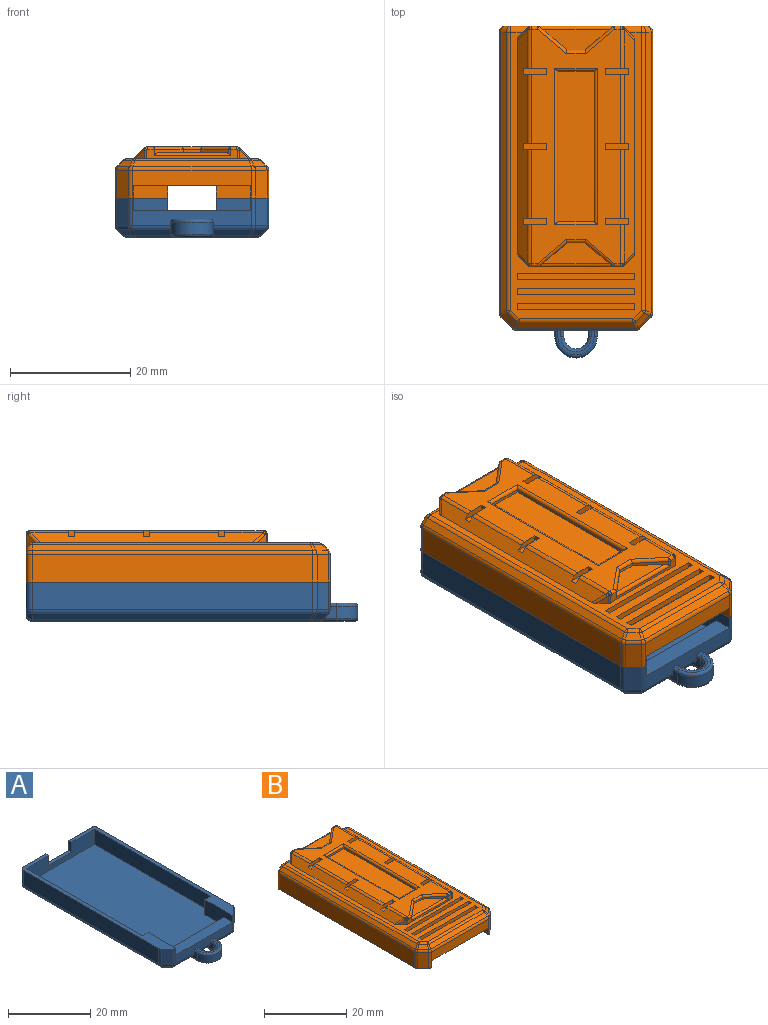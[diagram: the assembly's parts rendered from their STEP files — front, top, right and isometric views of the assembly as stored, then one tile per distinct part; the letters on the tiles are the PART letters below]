
ASSEMBLY  parts=2 mates=1
PART A: 149 faces, bbox 25.5x55.4x6.5 mm
  f0: plane 19.67x4.59mm, normal (0,-1,0), area 48.2mm2, adj f3,f4,f12,f14,f21,f22,f23,f35
  f1: plane 6.39x0.92mm, normal (0,-0.71,-0.71), area 8mm2, adj f3,f5,f62,f131,f137
  f2: plane 4.09x0.92mm, normal (0,-0.71,-0.71), area 5.2mm2, adj f4,f6,f132,f134,f140,f142
  f3: cylinder r=1mm len=6.34mm, axis (1,0,0), area 5mm2, adj f0,f1,f61,f131
  f4: cylinder r=1mm len=4mm, axis (1,0,0), area 3.1mm2, adj f0,f2,f132,f134
  f5: cylinder r=1mm len=6.46mm, axis (1,0,0), area 4.9mm2, adj f1,f7,f63,f137
  f6: cylinder r=1mm len=5mm, axis (1,0,0), area 3.5mm2, adj f2,f7,f140,f142
  f7: plane 53.59x21.67mm, normal (0,0,-1), area 887.7mm2, adj f5,f6,f38,f39,f40,f41,f42,f47
  f8: plane 40x4.5mm, normal (1,0,0), area 180mm2, adj f9,f14,f17,f25
  f9: plane 46.5x23.5mm, normal (0,0,1), area 1066.8mm2, adj f8,f10,f11,f17,f22,f23,f24,f25
  f10: plane 19.5x2.5mm, normal (0,1,0), area 48.7mm2, adj f9,f21,f22,f23
  f11: plane 40x4.5mm, normal (-1,0,0), area 180mm2, adj f9,f12,f17,f24
  f12: plane 50.5x8.75mm, normal (0,0,1), area 73.9mm2, adj f0,f11,f13,f15,f17,f20,f22,f24
  f13: plane 23.5x5.5mm, normal (0,1,0), area 104.4mm2, adj f12,f14,f18,f19,f20,f43,f45,f47
  f14: plane 50.5x8.75mm, normal (0,0,1), area 73.9mm2, adj f0,f8,f13,f16,f17,f19,f23,f25
  f15: plane 46.59x4.59mm, normal (1,0,0), area 213.6mm2, adj f12,f33,f51,f64
  f16: plane 46.59x4.59mm, normal (-1,0,0), area 213.6mm2, adj f14,f37,f43,f56
  f17: plane 23.5x4.5mm, normal (0,-1,0), area 81.7mm2, adj f8,f9,f11,f12,f14,f18,f19,f20
  f18: plane 8x1mm, normal (0,0,1), area 8mm2, adj f13,f17,f19,f20
  f19: plane 3x1mm, normal (1,0,0), area 3mm2, adj f13,f14,f17,f18
  f20: plane 3x1mm, normal (-1,0,0), area 3mm2, adj f12,f13,f17,f18
  f21: plane 19.5x3mm, normal (0,0,1), area 58.5mm2, adj f0,f10,f22,f23
  f22: plane 9.5x4.5mm, normal (-1,0,0), area 35.2mm2, adj f0,f9,f10,f12,f21,f24
  f23: plane 9.5x4.5mm, normal (1,0,0), area 35.2mm2, adj f0,f9,f10,f14,f21,f25
  f24: plane 4.5x2mm, normal (0,1,0), area 9mm2, adj f9,f11,f12,f22
  f25: plane 4.5x2mm, normal (0,1,0), area 9mm2, adj f8,f9,f14,f23
  f26: plane 4.59x1.91mm, normal (0.71,-0.71,0), area 12.4mm2, adj f12,f34,f52,f64
  f27: plane 4.59x1.91mm, normal (-0.71,-0.71,0), area 12.4mm2, adj f14,f36,f56,f60
  f28: plane 46.59x0.91mm, normal (0.71,0,-0.71), area 60mm2, adj f33,f42,f49,f66
  f29: plane 2.29x2.29mm, normal (0.5,-0.5,-0.71), area 3mm2, adj f34,f41,f54,f66
  f30: plane 6.39x0.92mm, normal (0,-0.71,-0.71), area 8mm2, adj f35,f40,f54,f135,f139
  f31: plane 46.59x0.91mm, normal (-0.71,0,-0.71), area 60mm2, adj f37,f38,f45,f58
  f32: plane 2.29x2.29mm, normal (-0.5,-0.5,-0.71), area 3mm2, adj f36,f39,f58,f62
  f33: cylinder r=1mm len=46.59mm, axis (0,1,0), area 36.6mm2, adj f15,f28,f50,f65
  f34: cylinder r=1mm len=2.12mm, axis (0.71,0.71,0), area 2.1mm2, adj f26,f29,f53,f65
  f35: cylinder r=1mm len=6.34mm, axis (1,0,0), area 5mm2, adj f0,f30,f53,f135
  f36: cylinder r=1mm len=2.12mm, axis (0.71,-0.71,0), area 2.1mm2, adj f27,f32,f57,f61
  f37: cylinder r=1mm len=46.59mm, axis (0,-1,0), area 36.6mm2, adj f16,f31,f44,f57
  f38: cylinder r=1mm len=46.21mm, axis (0,-1,0), area 36.3mm2, adj f7,f31,f46,f59
  f39: cylinder r=1mm len=1.88mm, axis (-0.71,0.71,0), area 1.5mm2, adj f7,f32,f59,f63
  f40: cylinder r=1mm len=6.46mm, axis (1,0,0), area 4.9mm2, adj f7,f30,f55,f139
  f41: cylinder r=1mm len=1.88mm, axis (0.71,0.71,0), area 1.5mm2, adj f7,f29,f55,f67
  f42: cylinder r=1mm len=46.21mm, axis (0,-1,0), area 36.3mm2, adj f7,f28,f48,f67
  f43: cylinder r=1mm len=4.59mm, axis (0,0,1), area 7.2mm2, adj f13,f14,f16,f44
  f44: sphere r=1mm, area 0.8mm2, adj f37,f43,f45
  f45: cylinder r=1mm len=1.62mm, axis (0.71,0,-0.71), area 2mm2, adj f13,f31,f44,f46
  f46: sphere r=1mm, area 0.8mm2, adj f38,f45,f47
  f47: cylinder r=1mm len=21.67mm, axis (-1,0,0), area 34mm2, adj f7,f13,f46,f48
  f48: sphere r=1mm, area 0.8mm2, adj f42,f47,f49
  f49: cylinder r=1mm len=1.62mm, axis (-0.71,0,-0.71), area 2mm2, adj f13,f28,f48,f50
  f50: sphere r=1mm, area 0.8mm2, adj f33,f49,f51
  f51: cylinder r=1mm len=4.59mm, axis (0,0,-1), area 7.2mm2, adj f12,f13,f15,f50
  f52: cylinder r=1mm len=4.59mm, axis (0,0,1), area 3.6mm2, adj f0,f12,f26,f53
  f53: sphere r=1mm, area 0.6mm2, adj f34,f35,f52,f54
  f54: cylinder r=1mm len=1.12mm, axis (0.28,-0.68,0.68), area 0.7mm2, adj f29,f30,f53,f55
  f55: sphere r=1mm, area 0.2mm2, adj f40,f41,f54
  f56: cylinder r=1mm len=4.59mm, axis (0,0,-1), area 3.6mm2, adj f14,f16,f27,f57
  f57: sphere r=1mm, area 0.6mm2, adj f36,f37,f56,f58
  f58: cylinder r=1mm len=1.12mm, axis (-0.68,-0.28,0.68), area 0.7mm2, adj f31,f32,f57,f59
  f59: sphere r=1mm, area 0.2mm2, adj f38,f39,f58
  f60: cylinder r=1mm len=4.59mm, axis (0,0,1), area 3.6mm2, adj f0,f14,f27,f61
  f61: sphere r=1mm, area 0.6mm2, adj f3,f36,f60,f62
  f62: cylinder r=1mm len=1.12mm, axis (0.28,0.68,-0.68), area 0.7mm2, adj f1,f32,f61,f63
  f63: sphere r=1mm, area 0.2mm2, adj f5,f39,f62
  f64: cylinder r=1mm len=4.59mm, axis (0,0,1), area 3.6mm2, adj f12,f15,f26,f65
  f65: sphere r=1mm, area 0.6mm2, adj f33,f34,f64,f66
  f66: cylinder r=1mm len=1.12mm, axis (-0.68,0.28,-0.68), area 0.7mm2, adj f28,f29,f65,f67
  f67: sphere r=1mm, area 0.2mm2, adj f41,f42,f66
  f68: plane 1.19x0.5mm, normal (1,0,0), area 0.6mm2, adj f7,f69,f79,f80
  f69: plane 4.93x3.64mm, normal (-0.59,-0.8,0), area 3.1mm2, adj f7,f68,f70,f80
  f70: plane 3.79x3.51mm, normal (0.68,-0.73,0), area 2.6mm2, adj f7,f69,f71,f80
  f71: plane 1.2x0.5mm, normal (-1,0,0), area 0.6mm2, adj f7,f70,f72,f80
  f72: plane 4.32x3.95mm, normal (-0.67,0.74,0), area 2.9mm2, adj f7,f71,f73,f80
  f73: plane 4.32x0.5mm, normal (0,-1,0), area 2.2mm2, adj f7,f72,f74,f80
  f74: plane 1.01x0.5mm, normal (-1,0,0), area 0.5mm2, adj f7,f73,f75,f80
  f75: plane 8.72x0.5mm, normal (0,1,0), area 4.4mm2, adj f7,f74,f76,f80
  f76: plane 1.01x0.5mm, normal (1,0,0), area 0.5mm2, adj f7,f75,f77,f80
  f77: plane 3.42x0.5mm, normal (0,-1,0), area 1.7mm2, adj f7,f76,f78,f80
  f78: plane 0.91x0.81mm, normal (0.75,-0.66,0), area 0.6mm2, adj f7,f77,f79,f80
  f79: plane 4.23x3.18mm, normal (0.6,0.8,0), area 2.6mm2, adj f7,f68,f78,f80
  f80: plane 8.72x6.3mm, normal (0,0,-1), area 20mm2, adj f68,f69,f70,f71,f72,f73,f74,f75
  f81: plane 2.5x0.5mm, normal (1,0,0), area 1.3mm2, adj f7,f82,f89,f126
  f82: plane 2.5x0.5mm, normal (0,1,0), area 1.3mm2, adj f7,f81,f89,f129
  f83: plane 5x0.5mm, normal (1,0,0), area 2.5mm2, adj f7,f89,f128,f129
  f84: plane 5x0.5mm, normal (0,-1,0), area 2.5mm2, adj f7,f89,f127,f128
  f85: plane 2.5x0.5mm, normal (-1,0,0), area 1.3mm2, adj f7,f86,f89,f127
  f86: plane 2.5x0.5mm, normal (0,-1,0), area 1.3mm2, adj f7,f85,f89,f125
  f87: plane 5x0.5mm, normal (-1,0,0), area 2.5mm2, adj f7,f89,f124,f125
  f88: plane 5x0.5mm, normal (0,1,0), area 2.5mm2, adj f7,f89,f124,f126
  f89: plane 10.5x10.5mm, normal (0,0,-1), area 84.5mm2, adj f81,f82,f83,f84,f85,f86,f87,f88
  f90: plane 8.72x0.5mm, normal (0,1,0), area 4.4mm2, adj f7,f91,f93,f94
  f91: plane 1.01x0.5mm, normal (1,0,0), area 0.5mm2, adj f7,f90,f92,f94
  f92: plane 8.72x0.5mm, normal (0,-1,0), area 4.4mm2, adj f7,f91,f93,f94
  f93: plane 1.01x0.5mm, normal (-1,0,0), area 0.5mm2, adj f7,f90,f92,f94
  f94: plane 8.72x1.01mm, normal (0,0,-1), area 8.8mm2, adj f90,f91,f92,f93
  f95: plane 4.86x0.5mm, normal (1,0,0), area 2.4mm2, adj f7,f96,f106,f107
  f96: plane 0.91x0.5mm, normal (0,-1,0), area 0.5mm2, adj f7,f95,f97,f107
  f97: plane 3.85x0.5mm, normal (-1,0,0), area 1.9mm2, adj f7,f96,f98,f107
  f98: plane 3.21x0.5mm, normal (0,-1,0), area 1.6mm2, adj f7,f97,f99,f107
  f99: plane 3.61x0.5mm, normal (1,0,0), area 1.8mm2, adj f7,f98,f100,f107
  f100: plane 0.9x0.5mm, normal (0,-1,0), area 0.4mm2, adj f7,f99,f101,f107
  f101: plane 3.61x0.5mm, normal (-1,0,0), area 1.8mm2, adj f7,f100,f102,f107
  f102: plane 2.81x0.5mm, normal (0,-1,0), area 1.4mm2, adj f7,f101,f103,f107
  f103: plane 3.85x0.5mm, normal (1,0,0), area 1.9mm2, adj f7,f102,f104,f107
  f104: plane 0.9x0.5mm, normal (0,-1,0), area 0.5mm2, adj f7,f103,f105,f107
  f105: plane 4.86x0.5mm, normal (-1,0,0), area 2.4mm2, adj f7,f104,f106,f107
  f106: plane 8.72x0.5mm, normal (0,1,0), area 4.4mm2, adj f7,f95,f105,f107
  f107: plane 8.72x4.86mm, normal (0,0,-1), area 19mm2, adj f95,f96,f97,f98,f99,f100,f101,f102
  f108: extruded ~2.27x0.96mm, area 1.3mm2, adj f7,f109,f122,f123
  f109: extruded ~1.98x0.5mm, area 1mm2, adj f7,f108,f110,f123
  f110: plane 0.87x0.5mm, normal (0.44,-0.9,0), area 0.5mm2, adj f7,f109,f111,f123
  f111: extruded ~2.4x0.5mm, area 1.2mm2, adj f7,f110,f112,f123
  f112: extruded ~2.24x0.55mm, area 1.2mm2, adj f7,f111,f113,f123
  f113: extruded ~1.56x1.46mm, area 1.1mm2, adj f7,f112,f114,f123
  f114: extruded ~2.36x0.5mm, area 1.2mm2, adj f7,f113,f115,f123
  f115: extruded ~3.32x1.05mm, area 1.8mm2, adj f7,f114,f116,f123
  f116: extruded ~2.97x1.17mm, area 1.6mm2, adj f7,f115,f117,f123
  f117: extruded ~2.24x0.5mm, area 1.1mm2, adj f7,f116,f118,f123
  f118: plane 0.89x0.5mm, normal (0,-1,0), area 0.4mm2, adj f7,f117,f119,f123
  f119: extruded ~2.08x0.5mm, area 1.1mm2, adj f7,f118,f120,f123
  f120: extruded ~2.29x0.93mm, area 1.3mm2, adj f7,f119,f121,f123
  f121: extruded ~2.64x0.8mm, area 1.4mm2, adj f7,f120,f122,f123
  f122: extruded ~2.62x0.83mm, area 1.4mm2, adj f7,f108,f121,f123
  f123: plane 8.96x6.6mm, normal (0,0,-1), area 16.6mm2, adj f108,f109,f110,f111,f112,f113,f114,f115
  f124: cylinder r=1mm len=1mm, axis (0,0,-1), area 0.8mm2, adj f7,f87,f88,f89
  f125: cylinder r=1mm len=1mm, axis (0,0,1), area 0.8mm2, adj f7,f86,f87,f89
  f126: cylinder r=1mm len=1mm, axis (0,0,1), area 0.8mm2, adj f7,f81,f88,f89
  f127: cylinder r=1mm len=1mm, axis (0,0,1), area 0.8mm2, adj f7,f84,f85,f89
  f128: cylinder r=1mm len=1mm, axis (0,0,-1), area 0.8mm2, adj f7,f83,f84,f89
  f129: cylinder r=1mm len=1mm, axis (0,0,1), area 0.8mm2, adj f7,f82,f83,f89
  f130: cylinder r=3.5mm len=7mm, axis (0,0,-1), area 22mm2, adj f131,f135,f138,f144
  f131: plane 2.09x2mm, normal (-1,0,0), area 2.7mm2, adj f0,f1,f3,f130,f137,f143
  f132: plane 2.09x2mm, normal (1,0,0), area 2.7mm2, adj f0,f2,f4,f133,f140,f146
  f133: cylinder r=2mm len=4mm, axis (0,0,-1), area 12.6mm2, adj f132,f134,f141,f147
  f134: plane 2.09x2mm, normal (-1,0,0), area 2.7mm2, adj f0,f2,f4,f133,f142,f148
  f135: plane 2.09x2mm, normal (1,0,0), area 2.7mm2, adj f0,f30,f35,f130,f139,f145
  f136: plane 6x4.09mm, normal (0,0,1), area 5.4mm2, adj f0,f143,f144,f145,f146,f147,f148
  f137: cylinder r=0.5mm len=3mm, axis (0,-1,0), area 2mm2, adj f1,f5,f7,f131,f138
  f138: torus R=3mm, axis (0,0,1), area 8.2mm2, adj f7,f130,f137,f139
  f139: cylinder r=0.5mm len=3mm, axis (0,1,0), area 2mm2, adj f7,f30,f40,f135,f138
  f140: cylinder r=0.5mm len=3mm, axis (0,1,0), area 2mm2, adj f2,f6,f7,f132,f141
  f141: torus R=2.5mm, axis (0,0,1), area 5.4mm2, adj f7,f133,f140,f142
  f142: cylinder r=0.5mm len=3mm, axis (0,-1,0), area 2mm2, adj f2,f6,f7,f134,f141
  f143: cylinder r=0.5mm len=1.09mm, axis (0,-1,0), area 0.9mm2, adj f0,f131,f136,f144
  f144: torus R=3mm, axis (0,0,-1), area 8.2mm2, adj f130,f136,f143,f145
  f145: cylinder r=0.5mm len=1.09mm, axis (0,1,0), area 0.9mm2, adj f0,f135,f136,f144
  f146: cylinder r=0.5mm len=1.09mm, axis (0,1,0), area 0.9mm2, adj f0,f132,f136,f147
  f147: torus R=2.5mm, axis (0,0,-1), area 5.4mm2, adj f133,f136,f146,f148
  f148: cylinder r=0.5mm len=1.09mm, axis (0,-1,0), area 0.9mm2, adj f0,f134,f136,f147
PART B: 173 faces, bbox 25.5x50.5x8.6 mm
  f0: plane 47.59x21.67mm, normal (0,0,1), area 215.5mm2, adj f4,f5,f29,f30,f31,f32,f33,f49
  f1: plane 19.67x4.59mm, normal (0,-1,0), area 51.2mm2, adj f2,f16,f24,f25,f26,f152,f164,f168
  f2: plane 50.5x8.75mm, normal (0,0,-1), area 73.9mm2, adj f1,f12,f17,f19,f20,f22,f26,f28
  f3: plane 39x14.67mm, normal (0,0,1), area 310.4mm2, adj f6,f7,f8,f9,f10,f11,f34,f35
  f4: plane 38.71x1.71mm, normal (0.71,0,0.71), area 86.3mm2, adj f0,f6,f7,f8,f34,f62,f78,f119
  f5: plane 38.71x1.71mm, normal (-0.71,0,0.71), area 86.3mm2, adj f0,f9,f10,f11,f35,f49,f69,f106
  f6: cylinder r=1mm len=11.5mm, axis (0,1,0), area 9mm2, adj f3,f4,f123,f126
  f7: cylinder r=1mm len=6.5mm, axis (0,1,0), area 5.1mm2, adj f3,f4,f81,f86,f122
  f8: cylinder r=1mm len=11.5mm, axis (0,1,0), area 9mm2, adj f3,f4,f119,f127
  f9: cylinder r=1mm len=11.5mm, axis (0,1,0), area 9mm2, adj f3,f5,f110,f114
  f10: cylinder r=1mm len=6.5mm, axis (0,1,0), area 5.1mm2, adj f3,f5,f50,f53,f112
  f11: cylinder r=1mm len=11.5mm, axis (0,1,0), area 9mm2, adj f3,f5,f108,f115
  f12: plane 40x4.5mm, normal (-1,0,0), area 180mm2, adj f2,f13,f20,f28
  f13: plane 46.5x23.5mm, normal (0,0,-1), area 1066.8mm2, adj f12,f14,f15,f20,f25,f26,f27,f28
  f14: plane 19.5x2.5mm, normal (0,1,0), area 48.7mm2, adj f13,f24,f25,f26
  f15: plane 40x4.5mm, normal (1,0,0), area 180mm2, adj f13,f16,f20,f27
  f16: plane 50.5x8.75mm, normal (0,0,-1), area 73.9mm2, adj f1,f15,f17,f18,f20,f23,f25,f27
  f17: plane 23.5x8mm, normal (0,1,0), area 129.3mm2, adj f2,f16,f21,f22,f23,f51,f53,f54
  f18: plane 46.59x4.59mm, normal (-1,0,0), area 213.6mm2, adj f16,f149,f153,f169
  f19: plane 46.59x4.59mm, normal (1,0,0), area 213.6mm2, adj f2,f148,f157,f171
  f20: plane 23.5x4.5mm, normal (0,-1,0), area 81.8mm2, adj f2,f12,f13,f15,f16,f21,f22,f23
  f21: plane 8x1mm, normal (0,0,-1), area 8mm2, adj f17,f20,f22,f23
  f22: plane 3x1mm, normal (-1,0,0), area 3mm2, adj f2,f17,f20,f21
  f23: plane 3x1mm, normal (1,0,0), area 3mm2, adj f16,f17,f20,f21
  f24: plane 19.5x3mm, normal (0,0,-1), area 58.5mm2, adj f1,f14,f25,f26
  f25: plane 9.5x4.5mm, normal (1,0,0), area 35.2mm2, adj f1,f13,f14,f16,f24,f27
  f26: plane 9.5x4.5mm, normal (-1,0,0), area 35.2mm2, adj f1,f2,f13,f14,f24,f28
  f27: plane 4.5x2mm, normal (0,1,0), area 9mm2, adj f13,f15,f16,f25
  f28: plane 4.5x2mm, normal (0,1,0), area 9mm2, adj f2,f12,f13,f26
  f29: plane 15.09x1.5mm, normal (0,-1,0), area 9.9mm2, adj f0,f43,f70,f73,f74,f76,f79,f82
  f30: plane 1.94x1.51mm, normal (0.71,0.71,0), area 1.8mm2, adj f0,f62,f64,f65,f141
  f31: plane 1.94x1.51mm, normal (-0.71,0.71,0), area 1.8mm2, adj f0,f49,f50,f51,f142
  f32: plane 1.51x1.51mm, normal (0.71,-0.71,0), area 1.6mm2, adj f0,f78,f81,f82
  f33: plane 1.51x1.51mm, normal (-0.71,-0.71,0), area 1.6mm2, adj f0,f69,f70,f71
  f34: cylinder r=1mm len=6.5mm, axis (0,1,0), area 5.1mm2, adj f3,f4,f65,f68,f120
  f35: cylinder r=1mm len=6.5mm, axis (0,1,0), area 5.1mm2, adj f3,f5,f71,f73,f106
  f36: plane 6x0.5mm, normal (0,1,0), area 3mm2, adj f37,f39,f40,f88
  f37: plane 25x0.5mm, normal (-1,0,0), area 12.5mm2, adj f36,f38,f40,f90
  f38: plane 6x0.5mm, normal (0,-1,0), area 3mm2, adj f37,f39,f40,f89
  f39: plane 25x0.5mm, normal (1,0,0), area 12.5mm2, adj f36,f38,f40,f87
  f40: plane 25x6mm, normal (0,0,1), area 150mm2, adj f36,f37,f38,f39
  f41: plane 4.63x3.88mm, normal (-0.64,-0.77,0), area 3.1mm2, adj f42,f44,f76,f79,f80
  f42: plane 2.97x0.5mm, normal (0,-1,0), area 1.5mm2, adj f41,f43,f44,f77
  f43: plane 4.77x4mm, normal (0.64,-0.77,0), area 3.2mm2, adj f29,f42,f44,f75,f76
  f44: plane 11.31x3.5mm, normal (0,0,1), area 25mm2, adj f41,f42,f43,f76
  f45: plane 4.63x3.88mm, normal (-0.64,0.77,0), area 3.1mm2, adj f47,f48,f59,f60,f61
  f46: plane 4.63x3.88mm, normal (0.64,0.77,0), area 3.1mm2, adj f47,f48,f56,f57,f59
  f47: plane 2.97x0.5mm, normal (0,1,0), area 1.5mm2, adj f45,f46,f48,f58
  f48: plane 11.31x3.5mm, normal (0,0,1), area 25mm2, adj f45,f46,f47,f59
  f49: cylinder r=0.5mm len=2.06mm, axis (-0.58,-0.58,-0.58), area 1.4mm2, adj f0,f5,f31,f50
  f50: bspline ~0.56x0.5mm, area 0.2mm2, adj f10,f31,f49,f52
  f51: cylinder r=0.5mm len=2.46mm, axis (0,0,-1), area 0.9mm2, adj f17,f31,f52,f142
  f52: sphere r=0.5mm, area 0.2mm2, adj f50,f51,f53
  f53: torus R=0.5mm, axis (0,-1,0), area 0.3mm2, adj f10,f17,f52,f54
  f54: cylinder r=0.5mm len=0.9mm, axis (-1,0,0), area 0.7mm2, adj f3,f17,f53,f55
  f55: sphere r=0.5mm, area 0.2mm2, adj f54,f56,f57
  f56: cylinder r=0.5mm len=5.09mm, axis (-0.77,0.64,0), area 4.8mm2, adj f3,f46,f55,f58
  f57: cylinder r=0.5mm len=1mm, axis (0,0,-1), area 0.3mm2, adj f17,f46,f55,f59
  f58: cylinder r=0.5mm len=3.33mm, axis (-1,0,0), area 2.4mm2, adj f3,f47,f56,f60
  f59: cylinder r=0.5mm len=12.86mm, axis (-1,0,0), area 9.5mm2, adj f17,f45,f46,f48,f57,f61
  f60: cylinder r=0.5mm len=5.09mm, axis (-0.77,-0.64,0), area 4.8mm2, adj f3,f45,f58,f63
  f61: cylinder r=0.5mm len=1mm, axis (0,0,-1), area 0.3mm2, adj f17,f45,f59,f63
  f62: cylinder r=0.5mm len=2.06mm, axis (-0.58,0.58,0.58), area 1.4mm2, adj f0,f4,f30,f65
  f63: sphere r=0.5mm, area 0.2mm2, adj f60,f61,f66
  f64: cylinder r=0.5mm len=2.46mm, axis (0,0,-1), area 0.9mm2, adj f17,f30,f67,f141
  f65: bspline ~0.56x0.5mm, area 0.2mm2, adj f30,f34,f62,f67
  f66: cylinder r=0.5mm len=0.9mm, axis (-1,0,0), area 0.7mm2, adj f3,f17,f63,f68
  f67: sphere r=0.5mm, area 0.2mm2, adj f64,f65,f68
  f68: torus R=0.5mm, axis (0,-1,0), area 0.3mm2, adj f17,f34,f66,f67
  f69: cylinder r=0.5mm len=2.06mm, axis (0.58,-0.58,0.58), area 1.4mm2, adj f0,f5,f33,f71
  f70: cylinder r=0.5mm len=1.46mm, axis (0,0,1), area 0.6mm2, adj f0,f29,f33,f72
  f71: bspline ~0.56x0.5mm, area 0.2mm2, adj f33,f35,f69,f72
  f72: sphere r=0.5mm, area 0.2mm2, adj f70,f71,f73
  f73: torus R=0.5mm, axis (0,1,0), area 0.3mm2, adj f29,f35,f72,f74
  f74: cylinder r=0.5mm len=1.09mm, axis (-1,0,0), area 0.8mm2, adj f3,f29,f73,f75
  f75: cylinder r=0.5mm len=5.23mm, axis (0.77,0.64,0), area 4.9mm2, adj f3,f43,f74,f77
  f76: cylinder r=0.5mm len=12.68mm, axis (-1,0,0), area 9.5mm2, adj f29,f41,f43,f44,f79
  f77: cylinder r=0.5mm len=3.33mm, axis (1,0,0), area 2.4mm2, adj f3,f42,f75,f80
  f78: cylinder r=0.5mm len=2.06mm, axis (0.58,0.58,-0.58), area 1.4mm2, adj f0,f4,f32,f81
  f79: cylinder r=0.5mm len=1mm, axis (0,0,1), area 0.3mm2, adj f29,f41,f76,f83
  f80: cylinder r=0.5mm len=5.09mm, axis (0.77,-0.64,0), area 4.8mm2, adj f3,f41,f77,f83
  f81: bspline ~0.56x0.5mm, area 0.2mm2, adj f7,f32,f78,f84
  f82: cylinder r=0.5mm len=1.46mm, axis (0,0,1), area 0.6mm2, adj f0,f29,f32,f84
  f83: sphere r=0.5mm, area 0.2mm2, adj f79,f80,f85
  f84: sphere r=0.5mm, area 0.2mm2, adj f81,f82,f86
  f85: cylinder r=0.5mm len=0.9mm, axis (-1,0,0), area 0.7mm2, adj f3,f29,f83,f86
  f86: torus R=0.5mm, axis (0,1,0), area 0.3mm2, adj f7,f29,f84,f85
  f87: cylinder r=0.5mm len=26mm, axis (0,1,0), area 19.9mm2, adj f3,f39,f88,f89
  f88: cylinder r=0.5mm len=7mm, axis (-1,0,0), area 5mm2, adj f3,f36,f87,f90
  f89: cylinder r=0.5mm len=7mm, axis (1,0,0), area 5mm2, adj f3,f38,f87,f90
  f90: cylinder r=0.5mm len=26mm, axis (0,-1,0), area 19.9mm2, adj f3,f37,f88,f89
  f91: plane 1x1mm, normal (1,0,0), area 1mm2, adj f0,f92,f94,f95
  f92: plane 19.5x1mm, normal (0,1,0), area 19.5mm2, adj f0,f91,f93,f95
  f93: plane 1x1mm, normal (-1,0,0), area 1mm2, adj f0,f92,f94,f95
  f94: plane 19.5x1mm, normal (0,-1,0), area 19.5mm2, adj f0,f91,f93,f95
  f95: plane 19.5x1mm, normal (0,0,1), area 19.5mm2, adj f91,f92,f93,f94
  f96: plane 1x1mm, normal (1,0,0), area 1mm2, adj f0,f97,f99,f100
  f97: plane 19.5x1mm, normal (0,1,0), area 19.5mm2, adj f0,f96,f98,f100
  f98: plane 1x1mm, normal (-1,0,0), area 1mm2, adj f0,f97,f99,f100
  f99: plane 19.5x1mm, normal (0,-1,0), area 19.5mm2, adj f0,f96,f98,f100
  f100: plane 19.5x1mm, normal (0,0,1), area 19.5mm2, adj f96,f97,f98,f99
  f101: plane 19.5x1mm, normal (0,1,0), area 19.5mm2, adj f0,f102,f104,f105
  f102: plane 1x1mm, normal (-1,0,0), area 1mm2, adj f0,f101,f103,f105
  f103: plane 19.5x1mm, normal (0,-1,0), area 19.5mm2, adj f0,f102,f104,f105
  f104: plane 1x1mm, normal (1,0,0), area 1mm2, adj f0,f101,f103,f105
  f105: plane 19.5x1mm, normal (0,0,1), area 19.5mm2, adj f101,f102,f103,f104
  f106: plane 3.91x1mm, normal (0,1,0), area 3.4mm2, adj f3,f5,f35,f107,f109
  f107: plane 1x1mm, normal (-1,0,0), area 1mm2, adj f3,f106,f108,f109
  f108: plane 3.91x1mm, normal (0,-1,0), area 3.4mm2, adj f3,f5,f11,f107,f109
  f109: plane 3.91x1mm, normal (0,0,1), area 3.9mm2, adj f5,f106,f107,f108
  f110: plane 3.91x1mm, normal (0,1,0), area 3.4mm2, adj f3,f5,f9,f111,f113
  f111: plane 1x1mm, normal (-1,0,0), area 1mm2, adj f3,f110,f112,f113
  f112: plane 3.91x1mm, normal (0,-1,0), area 3.4mm2, adj f3,f5,f10,f111,f113
  f113: plane 3.91x1mm, normal (0,0,1), area 3.9mm2, adj f5,f110,f111,f112
  f114: plane 3.91x1mm, normal (0,-1,0), area 3.4mm2, adj f3,f5,f9,f116,f117
  f115: plane 3.91x1mm, normal (0,1,0), area 3.4mm2, adj f3,f5,f11,f116,f117
  f116: plane 1x1mm, normal (-1,0,0), area 1mm2, adj f3,f114,f115,f117
  f117: plane 3.91x1mm, normal (0,0,1), area 3.9mm2, adj f5,f114,f115,f116
  f118: plane 1x1mm, normal (1,0,0), area 1mm2, adj f3,f119,f120,f121
  f119: plane 3.91x1mm, normal (0,1,0), area 3.4mm2, adj f3,f4,f8,f118,f121
  f120: plane 3.91x1mm, normal (0,-1,0), area 3.4mm2, adj f3,f4,f34,f118,f121
  f121: plane 3.91x1mm, normal (0,0,1), area 3.9mm2, adj f4,f118,f119,f120
  f122: plane 3.91x1mm, normal (0,1,0), area 3.4mm2, adj f3,f4,f7,f124,f125
  f123: plane 3.91x1mm, normal (0,-1,0), area 3.4mm2, adj f3,f4,f6,f124,f125
  f124: plane 1x1mm, normal (1,0,0), area 1mm2, adj f3,f122,f123,f125
  f125: plane 3.91x1mm, normal (0,0,1), area 3.9mm2, adj f4,f122,f123,f124
  f126: plane 3.91x1mm, normal (0,1,0), area 3.4mm2, adj f3,f4,f6,f128,f129
  f127: plane 3.91x1mm, normal (0,-1,0), area 3.4mm2, adj f3,f4,f8,f128,f129
  f128: plane 1x1mm, normal (1,0,0), area 1mm2, adj f3,f126,f127,f129
  f129: plane 3.91x1mm, normal (0,0,1), area 3.9mm2, adj f4,f126,f127,f128
  f130: plane 4.59x1.91mm, normal (0.71,-0.71,0), area 12.4mm2, adj f2,f150,f157,f164
  f131: plane 4.59x1.91mm, normal (-0.71,-0.71,0), area 12.4mm2, adj f16,f151,f153,f168
  f132: plane 46.59x0.91mm, normal (-0.71,0,0.71), area 60mm2, adj f143,f147,f149,f155
  f133: plane 2.29x2.29mm, normal (-0.5,-0.5,0.71), area 3mm2, adj f139,f151,f155,f166
  f134: plane 19.67x0.91mm, normal (0,-0.71,0.71), area 24.9mm2, adj f137,f152,f162,f166
  f135: plane 2.29x2.29mm, normal (0.5,-0.5,0.71), area 3mm2, adj f138,f150,f159,f162
  f136: plane 46.59x0.91mm, normal (0.71,0,0.71), area 60mm2, adj f140,f146,f148,f159
  f137: cylinder r=1mm len=18.91mm, axis (-1,0,0), area 14.9mm2, adj f0,f134,f161,f165
  f138: cylinder r=1mm len=1.88mm, axis (-0.71,-0.71,0), area 1.5mm2, adj f0,f135,f160,f161
  f139: cylinder r=1mm len=1.88mm, axis (0.71,-0.71,0), area 1.5mm2, adj f0,f133,f156,f165
  f140: cylinder r=1mm len=46.21mm, axis (0,-1,0), area 36.3mm2, adj f0,f136,f144,f160
  f141: cylinder r=1mm len=3.29mm, axis (1,0,0), area 4.3mm2, adj f0,f17,f30,f64,f144
  f142: cylinder r=1mm len=3.29mm, axis (1,0,0), area 4.3mm2, adj f0,f17,f31,f51,f145
  f143: cylinder r=1mm len=46.21mm, axis (0,-1,0), area 36.3mm2, adj f0,f132,f145,f156
  f144: sphere r=1mm, area 0.8mm2, adj f140,f141,f146
  f145: sphere r=1mm, area 0.8mm2, adj f142,f143,f147
  f146: cylinder r=1mm len=1.62mm, axis (-0.71,0,0.71), area 2mm2, adj f17,f136,f144,f172
  f147: cylinder r=1mm len=1.62mm, axis (0.71,0,0.71), area 2mm2, adj f17,f132,f145,f170
  f148: cylinder r=1mm len=46.59mm, axis (0,-1,0), area 36.6mm2, adj f19,f136,f158,f172
  f149: cylinder r=1mm len=46.59mm, axis (0,1,0), area 36.6mm2, adj f18,f132,f154,f170
  f150: cylinder r=1mm len=2.12mm, axis (-0.71,-0.71,0), area 2.1mm2, adj f130,f135,f158,f163
  f151: cylinder r=1mm len=2.12mm, axis (-0.71,0.71,0), area 2.1mm2, adj f131,f133,f154,f167
  f152: cylinder r=1mm len=19.67mm, axis (-1,0,0), area 15.5mm2, adj f1,f134,f163,f167
  f153: cylinder r=1mm len=4.59mm, axis (0,0,1), area 3.6mm2, adj f16,f18,f131,f154
  f154: sphere r=1mm, area 0.6mm2, adj f149,f151,f153,f155
  f155: cylinder r=1mm len=1.12mm, axis (-0.68,-0.28,-0.68), area 0.7mm2, adj f132,f133,f154,f156
  f156: sphere r=1mm, area 0.2mm2, adj f139,f143,f155
  f157: cylinder r=1mm len=4.59mm, axis (0,0,1), area 3.6mm2, adj f2,f19,f130,f158
  f158: sphere r=1mm, area 0.6mm2, adj f148,f150,f157,f159
  f159: cylinder r=1mm len=1.12mm, axis (0.68,-0.28,-0.68), area 0.7mm2, adj f135,f136,f158,f160
  f160: sphere r=1mm, area 0.2mm2, adj f138,f140,f159
  f161: sphere r=1mm, area 0.2mm2, adj f137,f138,f162
  f162: cylinder r=1mm len=1.12mm, axis (0.28,-0.68,-0.68), area 0.7mm2, adj f134,f135,f161,f163
  f163: sphere r=1mm, area 0.6mm2, adj f150,f152,f162,f164
  f164: cylinder r=1mm len=4.59mm, axis (0,0,1), area 3.6mm2, adj f1,f2,f130,f163
  f165: sphere r=1mm, area 0.2mm2, adj f137,f139,f166
  f166: cylinder r=1mm len=1.12mm, axis (0.28,0.68,0.68), area 0.7mm2, adj f133,f134,f165,f167
  f167: sphere r=1mm, area 0.6mm2, adj f151,f152,f166,f168
  f168: cylinder r=1mm len=4.59mm, axis (0,0,-1), area 3.6mm2, adj f1,f16,f131,f167
  f169: cylinder r=1mm len=4.59mm, axis (0,0,1), area 7.2mm2, adj f16,f17,f18,f170
  f170: sphere r=1mm, area 0.8mm2, adj f147,f149,f169
  f171: cylinder r=1mm len=4.59mm, axis (0,0,-1), area 7.2mm2, adj f2,f17,f19,f172
  f172: sphere r=1mm, area 0.8mm2, adj f146,f148,f171
PLACE A t=(2.68,-38.78,1.69)mm
PLACE B t=(28.18,-38.78,12.69)mm
MATE fastened A.f12 <-> B.f2  axis (0,0,1) through (25.18,-29.28,7.19)mm
